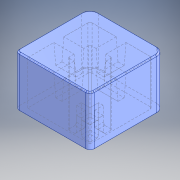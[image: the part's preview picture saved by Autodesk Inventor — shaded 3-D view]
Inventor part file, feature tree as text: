
AUTODESK INVENTOR PART (.ipt)
format: ipt  version: 2018 (Build 220112000, 112)  size: 378,880 bytes
history: native  units: in
note: dims shown in document units (in); Inventor stores cm internally (conversion verified against a paired STEP export)
features: other x15, fillet x4, projected_geometry x4, extrude x2, chamfer x2, loft x1, shell x1
ambient origin geometry x8: Origin, YZ Plane, XZ Plane, XY Plane, X Axis, Y Axis, Z Axis, Center Point
bodies: Solid1 (feature_tree)
feature tree (29):
  other  "Table"
  other  "Member = standard_cmx"
  other  "Member = smaller_cmx"
  other  "Member = larger_cmx"
  other  "Member = thumb_cmx"
  other  "Member = numbar_cmx"
  other  "BottomFace"
  other  "Top Plane"
  loft  "KeyCap Body"
  fillet  "Front Edge Rounding"  [1 undecoded]
  fillet  "Back Edge Rounding"  Radius=0.0in
  fillet  "Thumb Back-edge Rounding"  Radius=0.0394in
  shell  "Inner Keycap Shell"  Thickness=0.0591in
  extrude  "Pole Extrusion"  Depth=0.0394in
  extrude  "Cherry MX Cut in"  Depth=0.0787in
  other  "Ribbing Height Plane"
  other  "Ribbing Profiles"
  other  "Support Ribbing"
  chamfer  "Insert Assist Chamfer"  Distance=0.5906in
  chamfer  "Top Face Chamfer"  Distance=0.1575in
  fillet  "Cherry MX Pole Smoothing"  Radius=0.1969in
  other  "Base Plane"
  other  "TopFace"
  other  "Pole Base"
  projected_geometry  "Projected Loop1"
  other  "Cherry MX Cross"
  projected_geometry  "Projected Loop7"
  projected_geometry  "Projected Loop8"
  projected_geometry  "Projected Loop10"
note: 1 required parameter value undecoded (feature->parameter linkage not recoverable at this tier; creation-order binding heuristic only, values carry confidence <= 0.55)
